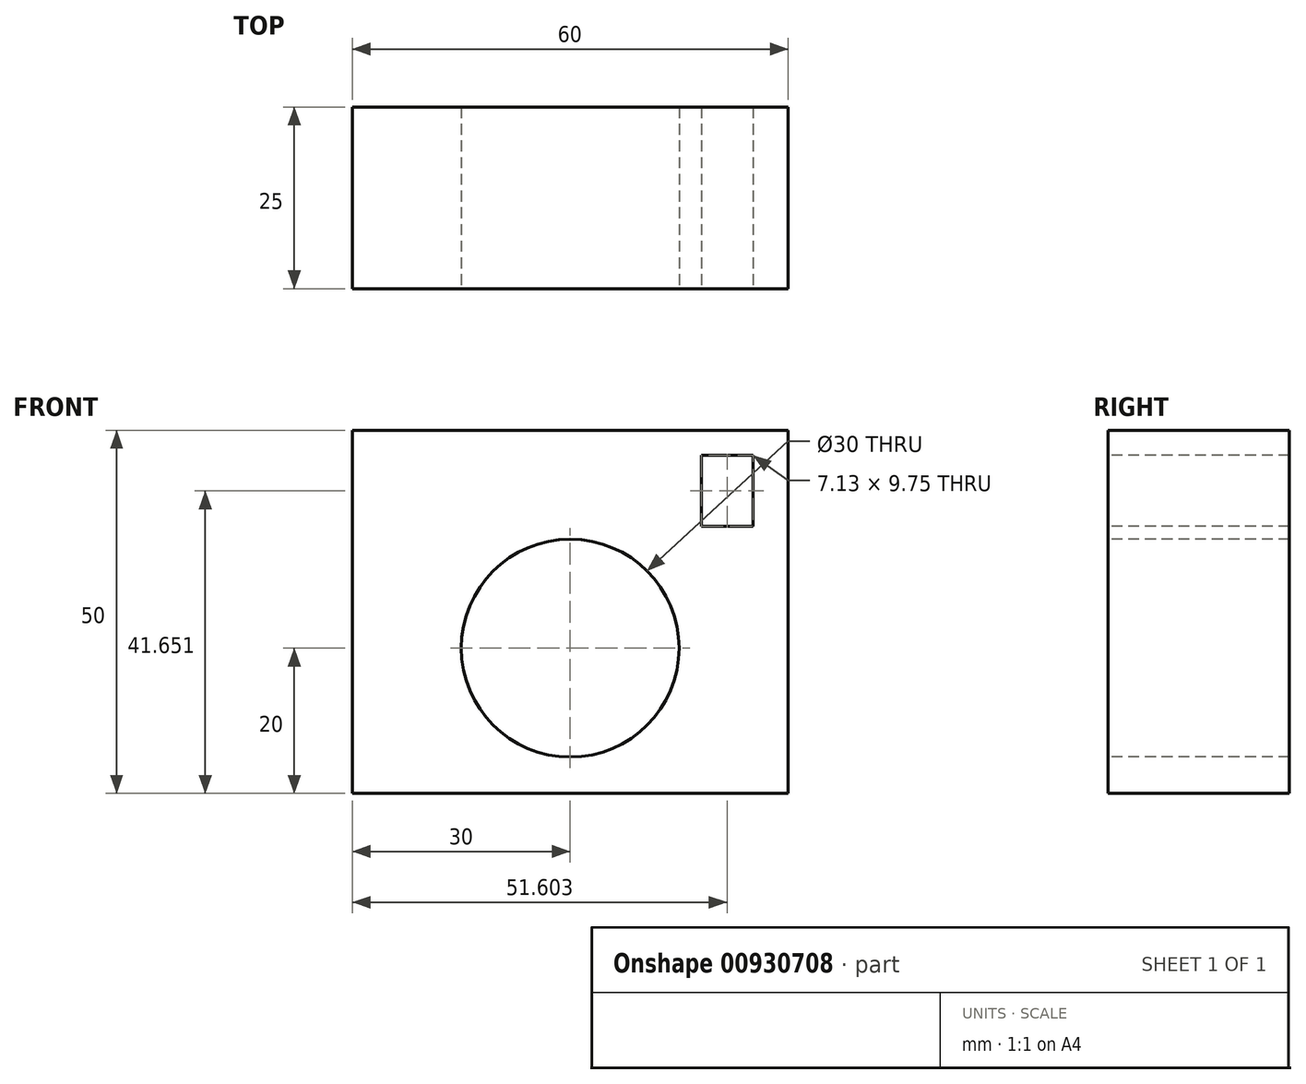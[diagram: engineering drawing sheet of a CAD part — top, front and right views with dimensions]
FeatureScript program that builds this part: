
annotation { "Feature Type Name" : "Feature", "Feature Type Description" : "" }
export const myFeature = defineFeature(function(context is Context, id is Id, definition is map)
    precondition{}
    {
        {
            var Q0;
            Q0=qCreatedBy(makeId("Front.planeOp"),FACE);
            var sketch = newSketch(context, id + "F0", { "sketchPlane" : qUnion([Q0])});
            skLineSegment(sketch, "E0.bottom", {"start": v(0, 0) * mm, "end": v(60, 0) * mm});
            skLineSegment(sketch, "E0.top", {"start": v(0, 50) * mm, "end": v(60, 50) * mm});
            skLineSegment(sketch, "E0.left", {"start": v(0, 0) * mm, "end": v(0, 50) * mm});
            skLineSegment(sketch, "E0.right", {"start": v(60, 0) * mm, "end": v(60, 50) * mm});
            skSolve(sketch);
        }
        {
            var Q0;
            Q0 = qSketchRegion(id + "F0", true);
            extrude(context, id + "F1", {"entities" : qUnion([Q0]), "depth" : 25 * mm, "offsetDistance" : 25 * mm});
        }
        {
            var Q0;
            Q0=makeQuery(id+"F1.opExtrude","CAP_FACE",FACE,{"disambiguationData":[OSD([sQuery(id+"F0.wireOp",EDGE,"E0.bottom"),sQuery(id+"F0.wireOp",EDGE,"E0.top"),sQuery(id+"F0.wireOp",EDGE,"E0.left"),sQuery(id+"F0.wireOp",EDGE,"E0.right")])],"isStart":false});
            var sketch = newSketch(context, id + "F2", { "sketchPlane" : qUnion([Q0])});
            skCircle(sketch, "E1", {"center": v(30, 20) * mm, "radius": 15 * mm});
            skSolve(sketch);
        }
        {
            var Q0;
            Q0 = qSketchRegion(id + "F2", true);
            extrude(context, id + "F3", {"entities" : qUnion([Q0]), "operationType" : NewBodyOperationType.REMOVE, "endBound" : BoundingType.THROUGH_ALL, "oppositeDirection" : true, "depth" : 25 * mm, "offsetDistance" : 25 * mm});
        }
        {
            var Q0;
            Q0=makeQuery(id+"F1.opExtrude","CAP_FACE",FACE,{"disambiguationData":[OSD([sQuery(id+"F0.wireOp",EDGE,"E0.bottom"),sQuery(id+"F0.wireOp",EDGE,"E0.top"),sQuery(id+"F0.wireOp",EDGE,"E0.left"),sQuery(id+"F0.wireOp",EDGE,"E0.right")])],"isStart":false});
            var sketch = newSketch(context, id + "F4", { "sketchPlane" : qUnion([Q0])});
            skLineSegment(sketch, "E2.bottom", {"start": v(48.04, 36.78) * mm, "end": v(55.17, 36.78) * mm});
            skLineSegment(sketch, "E2.top", {"start": v(48.04, 46.53) * mm, "end": v(55.17, 46.53) * mm});
            skLineSegment(sketch, "E2.left", {"start": v(48.04, 36.78) * mm, "end": v(48.04, 46.53) * mm});
            skLineSegment(sketch, "E2.right", {"start": v(55.17, 36.78) * mm, "end": v(55.17, 46.53) * mm});
            skSolve(sketch);
        }
        {
            var Q0;
            Q0 = qSketchRegion(id + "F4", true);
            extrude(context, id + "F5", {"entities" : qUnion([Q0]), "operationType" : NewBodyOperationType.REMOVE, "oppositeDirection" : true, "depth" : 25 * mm, "offsetDistance" : 25 * mm});
        }
    });
